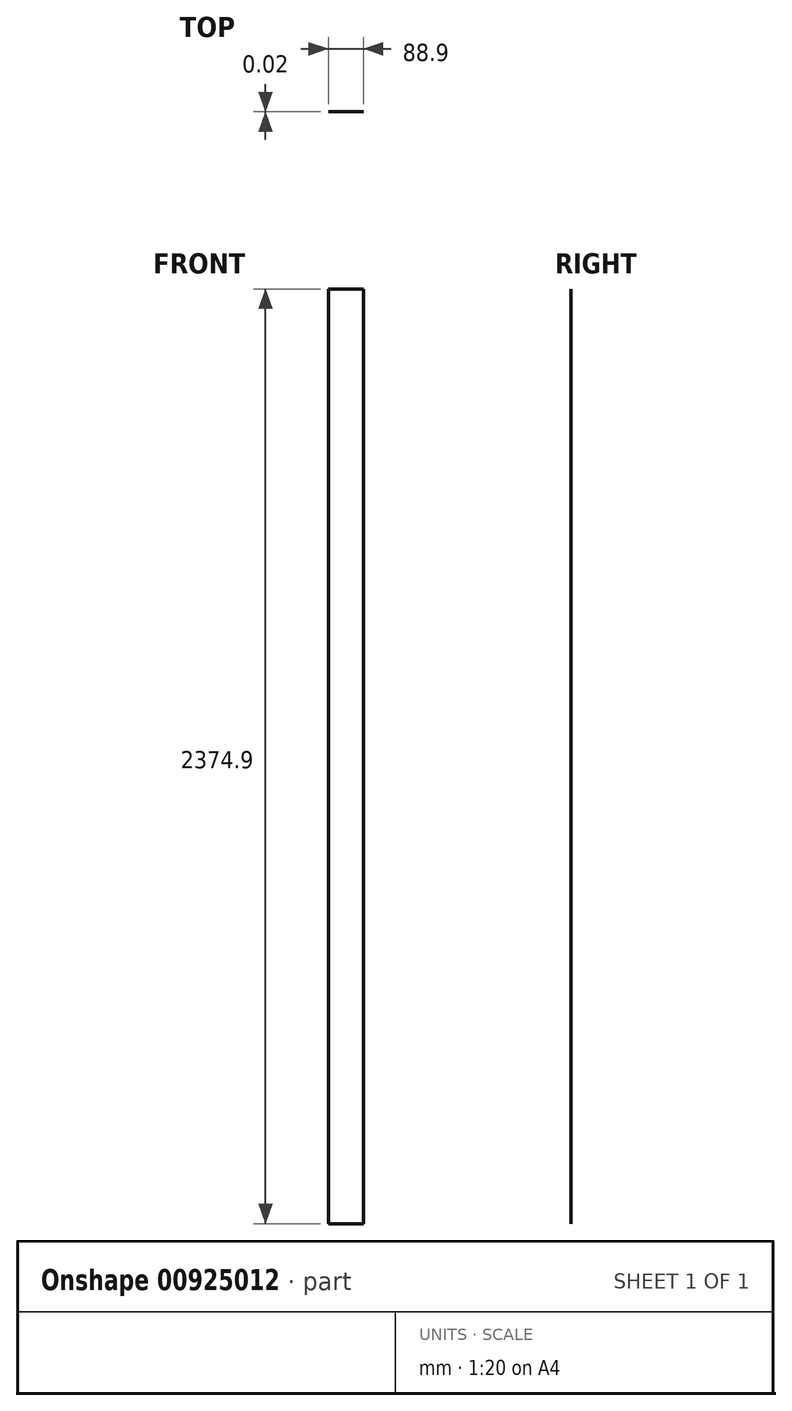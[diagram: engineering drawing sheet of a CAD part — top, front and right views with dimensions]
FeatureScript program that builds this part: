
annotation { "Feature Type Name" : "Feature", "Feature Type Description" : "" }
export const myFeature = defineFeature(function(context is Context, id is Id, definition is map)
    precondition{}
    {
        {
            assignVariable(context, id + "F0", {"name" : "length", "anyValue" : 93.5});
        }
        {
            var Q0;
            Q0=qCreatedBy(makeId("Front.planeOp"),FACE);
            var sketch = newSketch(context, id + "F1", { "sketchPlane" : qUnion([Q0])});
            skLineSegment(sketch, "E0.bottom", {"start": v(0, 0) * mm, "end": v(88.9, 0) * mm});
            skLineSegment(sketch, "E0.top", {"start": v(0, 2374.9) * mm, "end": v(88.9, 2374.9) * mm});
            skLineSegment(sketch, "E0.left", {"start": v(0, 0) * mm, "end": v(0, 2374.9) * mm});
            skLineSegment(sketch, "E0.right", {"start": v(88.9, 0) * mm, "end": v(88.9, 2374.9) * mm});
            skSolve(sketch);
        }
        {
            var Q0;
            Q0=qSketchRegion(id+"F1",true);
            extrude(context, id + "F2", {"entities" : qUnion([Q0]), "depth" : 5 / 203.2 * mm, "offsetDistance" : 25.4 * mm});
        }
        {
            var Q0;
            Q0=qCreatedBy(makeId("Top.planeOp"),FACE);
            var sketch = newSketch(context, id + "F3", { "sketchPlane" : qUnion([Q0])});
            skArc(sketch, "E1", {"start": v(34.93, -15.88) * mm, "mid": v(28.58, -9.52) * mm, "end": v(22.23, -15.88) * mm});
            skArc(sketch, "E2", {"start": v(66.68, -15.88) * mm, "mid": v(60.33, -9.52) * mm, "end": v(53.98, -15.88) * mm});
            skLineSegment(sketch, "E3", {"start": v(22.23, -15.88) * mm, "end": v(34.93, -15.88) * mm});
            skLineSegment(sketch, "E4", {"start": v(53.98, -15.88) * mm, "end": v(66.68, -15.88) * mm});
            skSolve(sketch);
        }
        {
            var Q0;
            Q0=makeQuery(id+"F3.imprint","IMPRINT",FACE,{"disambiguationData":[TD([[makeQuery(id+"F3.imprint","IMPRINT",EDGE,{"derivedFrom":sQuery(id+"F3.wireOp",EDGE,"E1")}),1.0]])]});
            var Q1;
            Q1=makeQuery(id+"F3.imprint","IMPRINT",FACE,{"disambiguationData":[TD([[makeQuery(id+"F3.imprint","IMPRINT",EDGE,{"derivedFrom":sQuery(id+"F3.wireOp",EDGE,"E2")}),1.0]])]});
            extrude(context, id + "F4", {"entities" : qUnion([Q0, Q1]), "operationType" : NewBodyOperationType.REMOVE, "depth" : (getVariable(context, 'length')) * mm, "offsetDistance" : 25.4 * mm});
        }
    });
